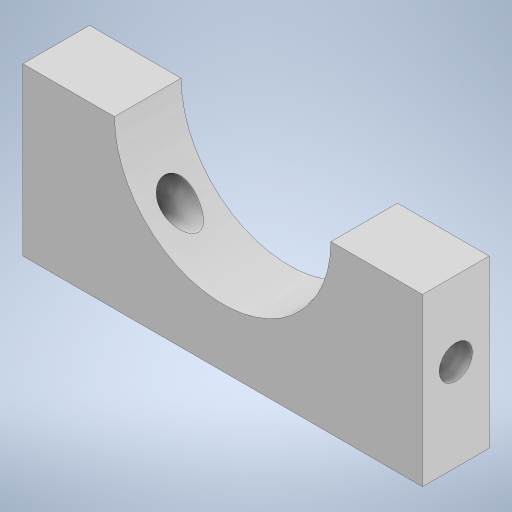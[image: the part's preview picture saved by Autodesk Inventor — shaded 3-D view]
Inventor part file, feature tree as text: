
AUTODESK INVENTOR PART (.ipt)
format: ipt  version: 2023 (Build 270158000, 158)  size: 219,648 bytes
history: native  units: in
note: dims shown in document units (in); Inventor stores cm internally (conversion verified against a paired STEP export)
features: extrude x2, sketch x2
ambient origin geometry x8: Origin, YZ Plane, XZ Plane, XY Plane, X Axis, Y Axis, Z Axis, Center Point
bodies: Body1 (feature_tree)
feature tree (4):
  extrude  "Extrusion4"  Depth=1.25in
  extrude  "Extrusion5"  Depth=0.25in
  sketch  "Sketch1"  dims[d21=1.25in d22=1.25in]
  sketch  "Sketch2"  dims[d23=0.5in d24=0.0in d26=0.25in d27=3.8125in d28=0.0in]
